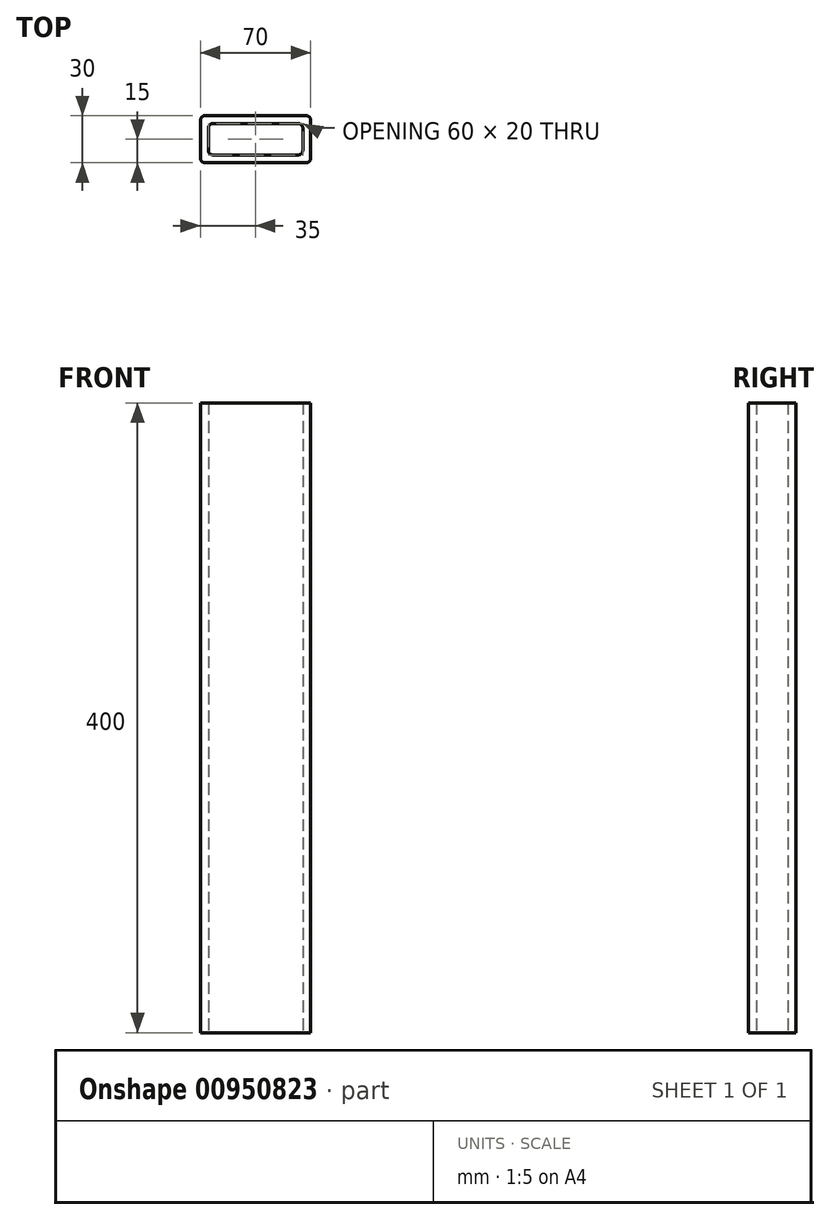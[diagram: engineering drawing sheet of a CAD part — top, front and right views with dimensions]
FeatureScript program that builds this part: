
annotation { "Feature Type Name" : "Feature", "Feature Type Description" : "" }
export const myFeature = defineFeature(function(context is Context, id is Id, definition is map)
    precondition{}
    {
        {
            var Q0;
            Q0=qCreatedBy(makeId("Top.planeOp"),FACE);
            var sketch = newSketch(context, id + "F0", { "sketchPlane" : qUnion([Q0])});
            skLineSegment(sketch, "E0.bottom", {"start": v(32, 15) * mm, "end": v(-32, 15) * mm});
            skLineSegment(sketch, "E0.top", {"start": v(32, -15) * mm, "end": v(-32, -15) * mm});
            skLineSegment(sketch, "E0.left", {"start": v(35, 12) * mm, "end": v(35, -12) * mm});
            skLineSegment(sketch, "E0.right", {"start": v(-35, 12) * mm, "end": v(-35, -12) * mm});
            skPoint(sketch, "E0.middle", {"position": v(0, 0) * mm});
            skLineSegment(sketch, "E1.bottom", {"start": v(27, 10) * mm, "end": v(-27, 10) * mm});
            skLineSegment(sketch, "E1.top", {"start": v(27, -10) * mm, "end": v(-27, -10) * mm});
            skLineSegment(sketch, "E1.left", {"start": v(30, 7) * mm, "end": v(30, -7) * mm});
            skLineSegment(sketch, "E1.right", {"start": v(-30, 7) * mm, "end": v(-30, -7) * mm});
            skPoint(sketch, "E2.visualSharp", {"position": v(-35, 15) * mm});
            skArc(sketch, "E2.filletArc", {"start": v(-32, 15) * mm, "mid": v(-34.12, 14.12) * mm, "end": v(-35, 12) * mm});
            skPoint(sketch, "E3.visualSharp", {"position": v(35, 15) * mm});
            skArc(sketch, "E3.filletArc", {"start": v(35, 12) * mm, "mid": v(34.12, 14.12) * mm, "end": v(32, 15) * mm});
            skPoint(sketch, "E4.visualSharp", {"position": v(35, -15) * mm});
            skArc(sketch, "E4.filletArc", {"start": v(32, -15) * mm, "mid": v(34.12, -14.12) * mm, "end": v(35, -12) * mm});
            skPoint(sketch, "E5.visualSharp", {"position": v(-35, -15) * mm});
            skArc(sketch, "E5.filletArc", {"start": v(-35, -12) * mm, "mid": v(-34.12, -14.12) * mm, "end": v(-32, -15) * mm});
            skPoint(sketch, "E6.visualSharp", {"position": v(30, 10) * mm});
            skArc(sketch, "E6.filletArc", {"start": v(30, 7) * mm, "mid": v(29.12, 9.12) * mm, "end": v(27, 10) * mm});
            skPoint(sketch, "E7.visualSharp", {"position": v(30, -10) * mm});
            skArc(sketch, "E7.filletArc", {"start": v(27, -10) * mm, "mid": v(29.12, -9.12) * mm, "end": v(30, -7) * mm});
            skPoint(sketch, "E8.visualSharp", {"position": v(-30, -10) * mm});
            skArc(sketch, "E8.filletArc", {"start": v(-30, -7) * mm, "mid": v(-29.12, -9.12) * mm, "end": v(-27, -10) * mm});
            skPoint(sketch, "E9.visualSharp", {"position": v(-30, 10) * mm});
            skArc(sketch, "E9.filletArc", {"start": v(-27, 10) * mm, "mid": v(-29.12, 9.12) * mm, "end": v(-30, 7) * mm});
            skSolve(sketch);
        }
        {
            var Q0;
            Q0=qSketchRegion(id+"F0",true);
            extrude(context, id + "F1", {"entities" : qUnion([Q0]), "depth" : 400 * mm, "offsetDistance" : 25 * mm});
        }
    });
